# Revit family: Deca_Chuveiro com desviador e ducha manual_Banho Competitivo_1965
name_source: partatom
category: Plumbing Fixtures
units: mm (PartAtom-declared; Revit-internal decimal feet)

## family parameters
Cut with Voids When Loaded = No
Host = Face
Part Type = Normal
Room Calculation Point = No
Round Connector Dimension = Use Radius
Shared = No

## types (1)
- 1965.C_Cromado
    Acompanha o Produto = Acompanha Parafuso e bucha para fixação
    Aprovado por = quattroD
    Atendimento ao Cliente = 0800-0117073
    Categoria = CHUVEIROS E DUCHAS
    Composição Anel Vedação = -
    Composição Assento = -
    Composição Básica = Liga cobre (bronze e latão),Aço,Plástico de Engenharia,Elastômeros
    Composição Componente = -
    Consumo = -
    Cor Interna = -
    Cor Principal = Cromado
    Cor Secundária = -
    Cores Componente = -
    Criado por = quattroD
    Código Pai = 1965
    Default Elevation = 2 m
    Description = Chuveiro com desviador e ducha manual
    Diâmetro Água Fria = 0 m
    Informações Complementares = -
    Itens de Instalação = -
    Linha = Banho Competitivo
    Manufacturer = Deca
    Material = Deca_Cromado
    Model = 1965.C
    Norma = NBR15206
    Peso Líquido (Kg) = 0.895
    Pressão máx. funcionamento = 40 MCA
    Pressão mín. Aquec. Acúmulo = 2 MCA
    Pressão mín. Aquec. Passagem = 4 MCA
    Pressão mín. funcionamento = 4 MCA
    Raio Água Fria = 0 m
    Saída de Esgoto = -
    Segmento = Banheiro Competitivo
    Tipo de dispositivo economizador = Sim
    Tipo de mecanismo utilizado = -
    Tipo de rosca de entrada = BSP NBR 8133
    Tipo de rosca de saída = -
    URL = www.deca.com.br
    Vazão na Pressão máx. (L/min) = 10.7
    Vazão na Pressão mín. (L/min) = 4.6

note: source unit labels omitted for Vazão na Pressão máx. (L/min), Vazão na Pressão mín. (L/min) — the stored unit's dimension contradicts the parameter name (converter mislabeling)

## geometry (parser evidence)
native form markers: Sweep x3
no freeform markers — native parametric forms only
